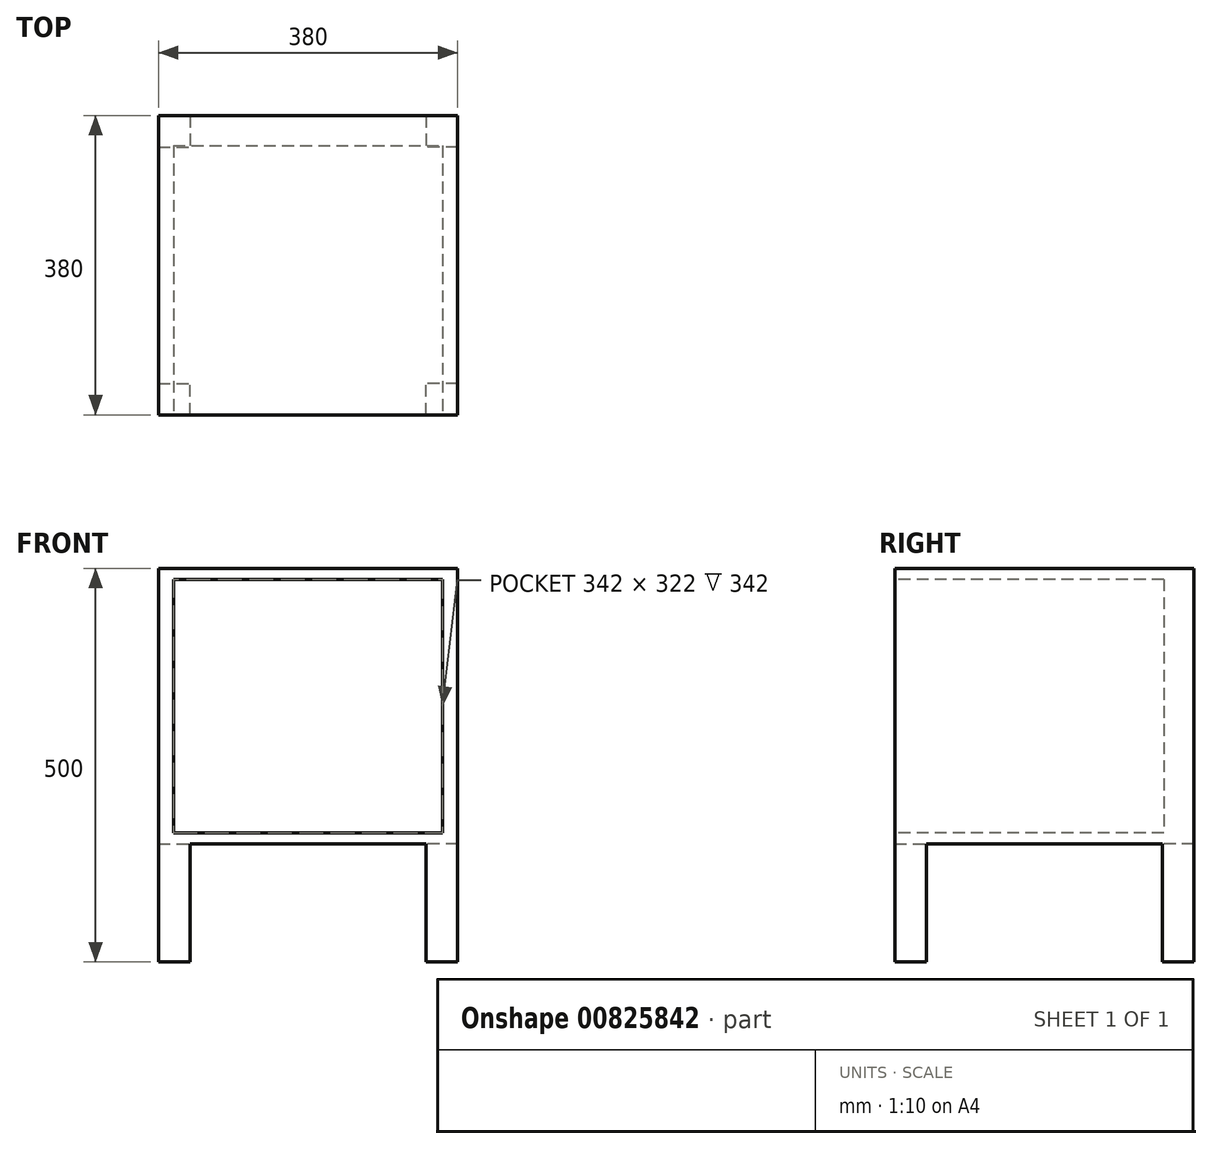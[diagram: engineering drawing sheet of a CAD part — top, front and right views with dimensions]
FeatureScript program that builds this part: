
annotation { "Feature Type Name" : "Feature", "Feature Type Description" : "" }
export const myFeature = defineFeature(function(context is Context, id is Id, definition is map)
    precondition{}
    {
        {
            var Q0;
            Q0=qCreatedBy(makeId("Top.planeOp"),FACE);
            var sketch = newSketch(context, id + "F0", { "sketchPlane" : qUnion([Q0])});
            skLineSegment(sketch, "E0.bottom", {"start": v(190, -190) * mm, "end": v(-190, -190) * mm});
            skLineSegment(sketch, "E0.top", {"start": v(190, 190) * mm, "end": v(-190, 190) * mm});
            skLineSegment(sketch, "E0.left", {"start": v(190, -190) * mm, "end": v(190, 190) * mm});
            skLineSegment(sketch, "E0.right", {"start": v(-190, -190) * mm, "end": v(-190, 190) * mm});
            skPoint(sketch, "E0.middle", {"position": v(0, 0) * mm});
            skSolve(sketch);
        }
        {
            var Q0;
            Q0 = qSketchRegion(id + "F0", true);
            extrude(context, id + "F1", {"entities" : qUnion([Q0]), "depth" : 350 * mm, "offsetDistance" : 25 * mm});
        }
        {
            var Q0;
            Q0=makeQuery(id+"F1.opExtrude","SWEPT_FACE",FACE,{"disambiguationData":[OSD([sQuery(id+"F0.wireOp",EDGE,"E0.bottom")])]});
            var sketch = newSketch(context, id + "F2", { "sketchPlane" : qUnion([Q0])});
            skLineSegment(sketch, "E1.bottom", {"start": v(-171, 336) * mm, "end": v(171, 336) * mm});
            skLineSegment(sketch, "E1.top", {"start": v(-171, 14) * mm, "end": v(171, 14) * mm});
            skLineSegment(sketch, "E1.left", {"start": v(-171, 336) * mm, "end": v(-171, 14) * mm});
            skLineSegment(sketch, "E1.right", {"start": v(171, 336) * mm, "end": v(171, 14) * mm});
            skPoint(sketch, "E1.middle", {"position": v(0, 175) * mm});
            skPoint(sketch, "E1.middle.positionSnap0", {"position": v(190, 175) * mm});
            skPoint(sketch, "E1.centerSnap0", {"position": v(190, 175) * mm});
            skSolve(sketch);
        }
        {
            var Q0;
            Q0 = qSketchRegion(id + "F2", true);
            extrude(context, id + "F3", {"entities" : qUnion([Q0]), "operationType" : NewBodyOperationType.REMOVE, "oppositeDirection" : true, "depth" : 342 * mm, "offsetDistance" : 25 * mm});
        }
        {
            var Q0;
            Q0=makeQuery(id+"F1.opExtrude","CAP_FACE",FACE,{"disambiguationData":[OSD([sQuery(id+"F0.wireOp",EDGE,"E0.bottom"),sQuery(id+"F0.wireOp",EDGE,"E0.top"),sQuery(id+"F0.wireOp",EDGE,"E0.left"),sQuery(id+"F0.wireOp",EDGE,"E0.right")])],"isStart":true});
            var sketch = newSketch(context, id + "F4", { "sketchPlane" : qUnion([Q0])});
            skLineSegment(sketch, "E2.bottom", {"start": v(-190, 190) * mm, "end": v(-150, 190) * mm});
            skLineSegment(sketch, "E2.top", {"start": v(-190, 150) * mm, "end": v(-150, 150) * mm});
            skLineSegment(sketch, "E2.left", {"start": v(-190, 190) * mm, "end": v(-190, 150) * mm});
            skLineSegment(sketch, "E2.right", {"start": v(-150, 190) * mm, "end": v(-150, 150) * mm});
            skSolve(sketch);
        }
        {
            var Q0;
            Q0=makeQuery(id+"F4.imprint","IMPRINT",FACE,{"disambiguationData":[TD([[makeQuery(id+"F4.imprint","IMPRINT",EDGE,{"derivedFrom":sQuery(id+"F4.wireOp",EDGE,"E2.bottom")}),1.0]])]});
            extrude(context, id + "F5", {"entities" : qUnion([Q0]), "operationType" : NewBodyOperationType.ADD, "depth" : 150 * mm, "offsetDistance" : 25 * mm});
        }
        {
            var Q0;
            Q0=makeQuery(id+"F1.opExtrude","CAP_FACE",FACE,{"disambiguationData":[OSD([sQuery(id+"F0.wireOp",EDGE,"E0.bottom"),sQuery(id+"F0.wireOp",EDGE,"E0.top"),sQuery(id+"F0.wireOp",EDGE,"E0.left"),sQuery(id+"F0.wireOp",EDGE,"E0.right")])],"isStart":true});
            var sketch = newSketch(context, id + "F6", { "sketchPlane" : qUnion([Q0])});
            skLineSegment(sketch, "E3.bottom", {"start": v(190, 190) * mm, "end": v(150, 190) * mm});
            skLineSegment(sketch, "E3.top", {"start": v(190, 150) * mm, "end": v(150, 150) * mm});
            skLineSegment(sketch, "E3.left", {"start": v(190, 190) * mm, "end": v(190, 150) * mm});
            skLineSegment(sketch, "E3.right", {"start": v(150, 190) * mm, "end": v(150, 150) * mm});
            skSolve(sketch);
        }
        {
            var Q0;
            Q0=makeQuery(id+"F6.imprint","IMPRINT",FACE,{"disambiguationData":[TD([[makeQuery(id+"F6.imprint","IMPRINT",EDGE,{"derivedFrom":sQuery(id+"F6.wireOp",EDGE,"E3.bottom")}),1.0]])]});
            extrude(context, id + "F7", {"entities" : qUnion([Q0]), "operationType" : NewBodyOperationType.ADD, "depth" : 150 * mm, "offsetDistance" : 25 * mm});
        }
        {
            var Q0;
            Q0=makeQuery(id+"F1.opExtrude","CAP_FACE",FACE,{"disambiguationData":[OSD([sQuery(id+"F0.wireOp",EDGE,"E0.bottom"),sQuery(id+"F0.wireOp",EDGE,"E0.top"),sQuery(id+"F0.wireOp",EDGE,"E0.left"),sQuery(id+"F0.wireOp",EDGE,"E0.right")])],"isStart":true});
            var sketch = newSketch(context, id + "F8", { "sketchPlane" : qUnion([Q0])});
            skLineSegment(sketch, "E4.bottom", {"start": v(-190, -190) * mm, "end": v(-150, -190) * mm});
            skLineSegment(sketch, "E4.top", {"start": v(-190, -150) * mm, "end": v(-150, -150) * mm});
            skLineSegment(sketch, "E4.left", {"start": v(-190, -190) * mm, "end": v(-190, -150) * mm});
            skLineSegment(sketch, "E4.right", {"start": v(-150, -190) * mm, "end": v(-150, -150) * mm});
            skSolve(sketch);
        }
        {
            var Q0;
            Q0=makeQuery(id+"F8.imprint","IMPRINT",FACE,{"disambiguationData":[TD([[makeQuery(id+"F8.imprint","IMPRINT",EDGE,{"derivedFrom":sQuery(id+"F8.wireOp",EDGE,"E4.bottom")}),-1.0]])]});
            extrude(context, id + "F9", {"entities" : qUnion([Q0]), "operationType" : NewBodyOperationType.ADD, "depth" : 150 * mm, "offsetDistance" : 25 * mm});
        }
        {
            var Q0;
            Q0=makeQuery(id+"F1.opExtrude","CAP_FACE",FACE,{"disambiguationData":[OSD([sQuery(id+"F0.wireOp",EDGE,"E0.bottom"),sQuery(id+"F0.wireOp",EDGE,"E0.top"),sQuery(id+"F0.wireOp",EDGE,"E0.left"),sQuery(id+"F0.wireOp",EDGE,"E0.right")])],"isStart":true});
            var sketch = newSketch(context, id + "F10", { "sketchPlane" : qUnion([Q0])});
            skLineSegment(sketch, "E5.bottom", {"start": v(190, -190) * mm, "end": v(150, -190) * mm});
            skLineSegment(sketch, "E5.top", {"start": v(190, -150) * mm, "end": v(150, -150) * mm});
            skLineSegment(sketch, "E5.left", {"start": v(190, -190) * mm, "end": v(190, -150) * mm});
            skLineSegment(sketch, "E5.right", {"start": v(150, -190) * mm, "end": v(150, -150) * mm});
            skSolve(sketch);
        }
        {
            var Q0;
            Q0=makeQuery(id+"F10.imprint","IMPRINT",FACE,{"disambiguationData":[TD([[makeQuery(id+"F10.imprint","IMPRINT",EDGE,{"derivedFrom":sQuery(id+"F10.wireOp",EDGE,"E5.bottom")}),-1.0]])]});
            extrude(context, id + "F11", {"entities" : qUnion([Q0]), "operationType" : NewBodyOperationType.ADD, "depth" : 150 * mm, "offsetDistance" : 25 * mm});
        }
    });
